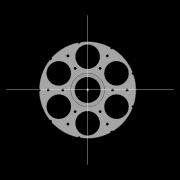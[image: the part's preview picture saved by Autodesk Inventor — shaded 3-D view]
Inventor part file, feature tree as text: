
AUTODESK INVENTOR PART (.ipt)
format: ipt  version: 2022.2 (Build 262287010, 287A)  size: 693,760 bytes
history: native  units: mm
features: other x20, extrude x17, sketch x12, pattern_circular x7, plane x4, fillet x2, move_body x2, revolve x2, draft x2, chamfer x2
ambient origin geometry x8: Origin, YZ Plane, XZ Plane, XY Plane, X Axis, Y Axis, Z Axis, Center Point
bodies: Solid5 (feature_tree)
feature tree (70):
  other  "CrossSection1"
  sketch  "Sketch7"  dims[d90=15.767323mm]
  other  "Roller1"
  other  "Roller2"
  sketch  "Sketch22"  dims[d167=8.972256mm]
  sketch  "Sketch2"  dims[d57=4.025mm]
  sketch  "Sketch23"  dims[d173=10.814812mm]
  other  "RevRoller1"
  fillet  "Fillet1"  Radius=13.336791mm
  pattern_circular  "Circular Pattern13"  Count=360  [1 undecoded]
  move_body  "Move Body7"
  revolve  "Revolution13"  [1 undecoded]
  fillet  "Fillet3"  Radius=0.025mm
  pattern_circular  "Circular Pattern14"  [2 undecoded]
  move_body  "Move Body6"
  revolve  "Revolution14"  [1 undecoded]
  other  "OuterRim_Top2"
  other  "OuterRim_Bottom2"
  extrude  "Rotor_Ring"  Depth=1.0mm
  draft  "FaceDraft2"
  sketch  "Sketch30"  dims[d201=53.5mm d232=0.0mm d233=3600.0mm]
  plane  "Work Plane5"
  other  "Rotor Featurs"
  other  "RotorRim_Bottom"
  extrude  "Extrusion24"  Depth=1.0mm
  extrude  "Extrusion25"  Depth=1.0mm
  extrude  "Extrusion26"  TaperAngle=90.0deg  [1 undecoded]
  pattern_circular  "Circular Pattern23"  [2 undecoded]
  sketch  "Sketch41"  dims[d346=0.025mm]
  extrude  "Extrusion27"  Depth=1.0mm
  extrude  "Extrusion28"  TaperAngle=360.0deg  [1 undecoded]
  pattern_circular  "Circular Pattern24"  Angle=30.0deg  [1 undecoded]
  extrude  "Extrusion29"  Depth=1.0mm
  extrude  "Extrusion30"  Depth=1.0mm
  extrude  "Extrusion31"  Depth=1.0mm
  pattern_circular  "Circular Pattern25"  [2 undecoded]
  sketch  "Sketch42"  dims[d347=0.1mm]
  extrude  "Extrusion32"  TaperAngle=30.0deg  [1 undecoded]
  extrude  "Extrusion33"  TaperAngle=90.0deg  [1 undecoded]
  extrude  "Extrusion34"  Depth=1.0mm
  extrude  "Extrusion35"  Depth=1.0mm
  pattern_circular  "Circular Pattern26"  Angle=360.0deg  [1 undecoded]
  pattern_circular  "Circular Pattern27"  Angle=90.0deg  [1 undecoded]
  chamfer  "Chamfer1"  Distance=0.1mm
  chamfer  "Chamfer2"  Distance=0.025mm
  draft  "FaceDraft4"
  plane  "Work Plane7"
  sketch  "Sketch44"  dims[d349=17.374602mm]
  sketch  "Sketch45"  dims[d350=17.374329mm]
  extrude  "Extrusion39"  Depth=1.0mm
  extrude  "Extrusion40"  Depth=1.0mm
  plane  "Work Plane8"
  sketch  "Sketch46"  dims[d351=0.025mm d352=0.025mm d354=0.025mm d355=17.374329mm d356=17.374602mm d357=1.0mm d358=90.0deg d359=0.5mm d360=60.0mm d361=360.0deg d363=30.0deg d367=8.1mm d369=4.014775mm d370=0.025mm d371=1.0mm d372=30.0deg d373=90.0deg d374=0.5mm d375=60.0mm d376=360.0deg d378=90.0deg d379=0.1mm d380=0.025mm d381=0.025mm d382=0.025mm d383=0.025mm d384=10.461905mm d385=0.0mm d386=0.0mm d391=1.0mm d392=53.5mm d393=1.5mm d394=1.5mm d395=1.5mm d396=1.5mm d397=90.0deg d398=90.0deg d399=90.0deg d400=53.5mm d401=10.461905mm d402=0.0mm d486=0.436332mm d487=0.5mm d488=2.0mm d489=0.0mm d490=20.0mm d495=2.5mm d496=8.0mm d506=13.856406mm d507=55.5mm d508=8.0mm d509=0.05mm d510=2.5mm d511=30.0deg d512=12.0mm d513=6.0mm d514=0.2mm d515=30.0deg d516=131.0mm d517=65.5mm d518=0.2mm d519=100.0mm d520=120.0mm d521=2.0mm d522=150.0mm d530=50.0mm d531=5.5mm d532=5.5mm d533=5.5mm d534=87.0mm d535=73.5mm d536=55.0mm d537=27.0mm d538=3.0mm d539=2.4mm d540=0.0mm d541=0.0mm d542=0.0mm d543=5.5mm d544=3.0mm d545=0.0mm d546=90.0mm d547=360.0deg d549=3.0mm d550=3.0mm d551=2.4mm d552=0.0mm d553=5.230953mm d554=0.0mm d555=2.4mm d556=0.0mm d557=5.230953mm d558=0.0mm d559=5.230953mm d560=0.0mm d561=90.0mm d562=360.0deg d564=60.0mm d565=360.0deg d567=5.5mm d568=5.5mm d569=3.0mm d570=0.0mm d571=5.230953mm d572=0.0mm d573=3.0mm d574=0.0mm d575=5.230953mm d576=0.0mm d577=90.0mm d578=360.0deg d580=60.0mm d581=360.0deg d584=20.0mm d585=8.0mm d587=1.75mm d589=3.0mm d592=2.0mm d593=12.0mm d594=12.0mm d600=0.5mm d601=2.0mm d602=45.0deg d603=0.5mm d604=2.0mm d605=45.0deg d606=0.436332mm d607=0.5mm d608=0.0mm d609=20.0mm d611=360.0deg d613=0.0mm d614=0.0mm d615=50.0mm d617=1.0mm d618=3.0mm d619=20.0mm d621=360.0deg d623=0.8mm d624=0.0mm d625=0.8mm d626=0.0mm d627=20.0mm d635=12.0mm d640=2.5mm d641=100.0mm d643=360.0deg d645=0.0mm d646=3600.0mm d16=0.872665mm d17=0.872665mm d49=0.872665mm d50=0.872665mm d51=0.872665mm d52=0.872665mm d236=0.5mm d237=0.872665mm d238=0.5mm d239=0.872665mm d282=1.0mm d283=1.0mm d284=1.0mm d285=0.15mm d286=0.25mm d287=0.375mm d288=14.3117mm d289=0.75mm d290=20.594885mm d291=0.0625mm d292=0.75mm d293=0.375mm d405=0.5mm d406=0.872665mm d407=0.5mm d408=0.872665mm d413=0.5mm d414=0.872665mm d415=0.5mm d416=0.872665mm d417=0.5mm d418=0.872665mm d419=0.5mm d420=0.872665mm d421=0.872665mm d431=0.5mm d432=0.872665mm d433=0.5mm d434=0.872665mm d471=0.5mm d472=0.872665mm d473=0.5mm d474=0.872665mm d497=0.5mm d498=0.872665mm d499=0.5mm d500=0.872665mm d590=0.5mm d591=0.872665mm]
  plane  "Work Plane6"
  sketch  "Sketch43"  dims[d348=0.1mm]
  extrude  "Extrusion37"  Depth=1.0mm
  extrude  "Extrusion38"  Depth=1.0mm
  other  "2D Equation Curve1"
  sketch  "Sketch40"  dims[d343=17.374329mm d344=17.374602mm d345=0.025mm]
  other  "Work Axis6"
  other  "Work Axis7"
  other  "Work Axis8"
  other  "Work Axis9"
  other  "Work Axis10"
  other  "Work Point1"
  other  "Work Point2"
  other  "Work Point3"
  other  "Work Point4"
  other  "Work Point5"
  other  "2D Equation Curve2"
note: 16 required parameter values undecoded (feature->parameter linkage not recoverable at this tier; creation-order binding heuristic only, values carry confidence <= 0.55)